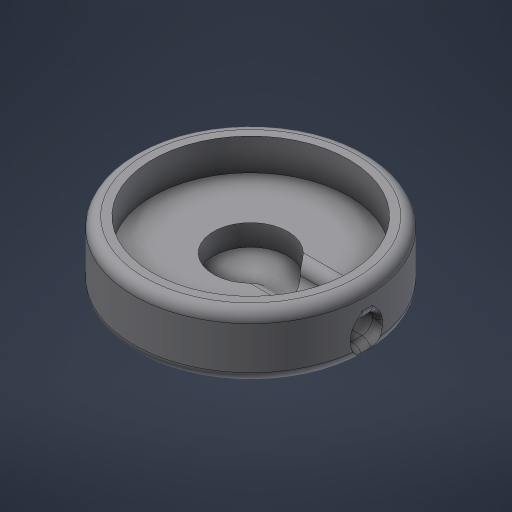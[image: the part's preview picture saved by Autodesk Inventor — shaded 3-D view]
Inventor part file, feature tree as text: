
AUTODESK INVENTOR PART (.ipt)
format: ipt  version: 2023.5 (Build 275446000, 446)  size: 654,848 bytes
history: native  units: mm
features: extrude x3, sketch x1, fillet x1
ambient origin geometry x8: Origin, YZ Plane, XZ Plane, XY Plane, X Axis, Y Axis, Z Axis, Center Point
bodies: Volumenkörper1 (feature_tree)
feature tree (5):
  sketch  "Skizze1"  dims[d0=18.5mm d1=7.0mm d2=3.0mm d3=22.0mm d4=3.0mm d5=0.0mm d6=3.0mm d7=0.0mm d8=2.0mm d9=0.0mm d10=1.0mm]
  extrude  "Extrusion1"  Depth=7.0mm
  extrude  "Extrusion2"  Depth=3.0mm
  extrude  "Extrusion3"  Depth=22.0mm
  fillet  "Rundung1"  Radius=3.0mm
